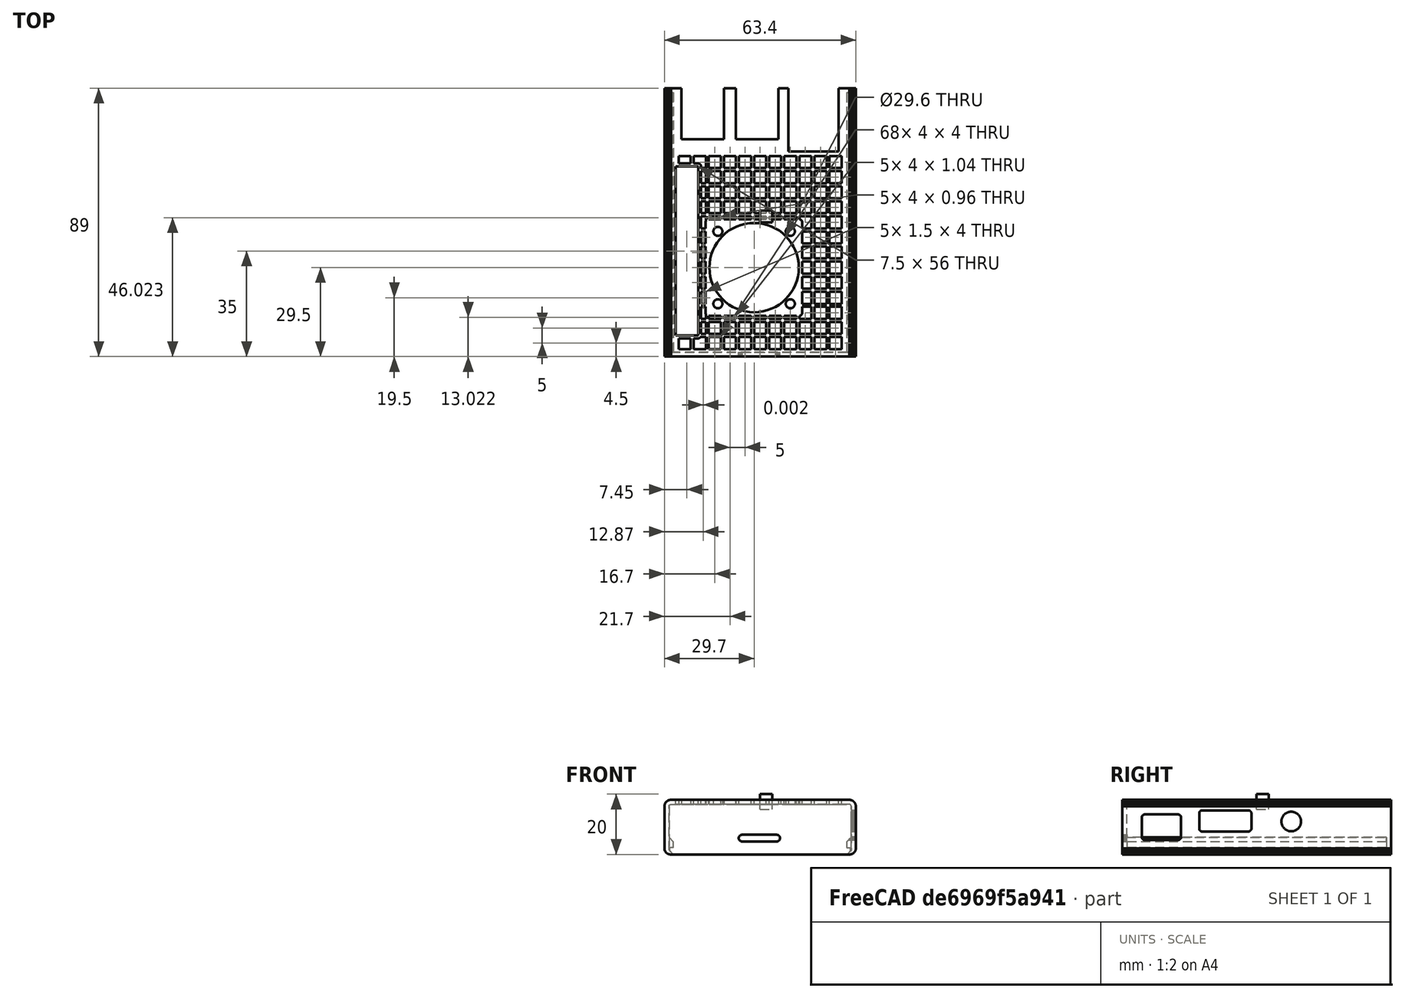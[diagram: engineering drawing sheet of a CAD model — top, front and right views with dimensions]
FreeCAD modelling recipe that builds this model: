
FCSTD DOCUMENT  (FreeCAD 0.14R3702 (Git))
Label: mi_raspberry_case
License: CC-BY 3.0
LicenseURL: http://creativecommons.org/licenses/by/3.0/
objects: Part::Feature×7, Part::MultiFuse×7, Part::Box×5, Mesh::Feature×3, Part::Offset×2, Part::Cut×2, Part::MultiCommon×1, Part::Cylinder×1, Part::FeaturePython×1
note: 26 computed .brp shape members not serialized (recipe doc carries the construction recipe); baked Part::Feature solids carry a one-line shape summary decoded from their .brp

FEATURE [Mesh::Feature] Raspberry_Pi_2_Case_v1_0___Cover  label="Raspberry_Pi_2_Case_v1.0_-_Cover"
FEATURE [Mesh::Feature] COVER_FAN_30X30
  Placement = pos=(-2,-15,18) rot=(0,0,1;0rad)
FEATURE [Mesh::Feature] B__Model_v4  label="B+_Model_v4"
  Placement = pos=(70.5,97,2) rot=(0,0,1;1.5708rad)
FEATURE [Part::Feature] Raspberry_Pi_2_Case_v1_0___Cover001
  shape: bbox 63.4 x 89 x 18.1 mm, 3440 faces, 0 solids (baked)
FEATURE [Part::Feature] Raspberry_Pi_2_Case_v1_0___Cover001001  label="Raspberry_Pi_2_Case_v1_0___Cover002"
  shape: bbox 63.4 x 89 x 18.1 mm, 1022 faces, 0 solids (baked)
FEATURE [Part::Feature] Raspberry_Pi_2_Case_v1_0___Cover001001_solid  label="Raspberry_Pi_2_Case_v1_0___Cover002 (Solid)"
  shape: bbox 63.4 x 89 x 18.1 mm, 1022 faces (baked)
FEATURE [Part::Box] Box  label="hueco gpio"
  Height = 5
  Length = 7.5
  Placement = pos=(-28,-37.5,13) rot=(0,0,1;0rad)
  Width = 56
FEATURE [Part::Box] Box001  label="caja ventilador"
  Height = 5
  Length = 30
  Placement = pos=(-17,-30,13) rot=(0,0,1;0rad)
  Width = 30
FEATURE [Part::Feature] Part__Feature  label="Chamfer001"
  Placement = pos=(-14,-3,20) rot=(0,0,1;0rad)
  shape: bbox 5.5 x 5.5 x 15 mm, 16 faces (baked)
FEATURE [Part::Feature] Part__Feature001  label="Chamfer002"
  Placement = pos=(10,-3,20) rot=(0,0,1;0rad)
  shape: bbox 5.5 x 5.5 x 15 mm, 16 faces (baked)
FEATURE [Part::MultiFuse] Fusion
  Shapes = -> [Part__Feature001,Part__Feature]
FEATURE [Part::Feature] Part__Feature002  label="Chamfer003"
  Placement = pos=(-14,-3,20) rot=(0,0,1;0rad)
  shape: bbox 5.5 x 5.5 x 15 mm, 16 faces (baked)
FEATURE [Part::Feature] Part__Feature003  label="Chamfer004"
  Placement = pos=(10,-3,20) rot=(0,0,1;0rad)
  shape: bbox 5.5 x 5.5 x 15 mm, 16 faces (baked)
FEATURE [Part::MultiFuse] Fusion001
  Placement = pos=(0,-24,0) rot=(0,0,1;0rad)
  Shapes = -> [Part__Feature003,Part__Feature002]
FEATURE [Part::MultiFuse] Fusion002  label="tornillos"
  Shapes = -> [Fusion001,Fusion]
FEATURE [Part::Box] Box002  label="Cubo"
  Height = 5
  Length = 4
  Placement = pos=(0,0,13) rot=(0,0,1;0rad)
  Width = 4
FEATURE [Part::Box] Box003  label="hueco gpio001"
  Height = 5
  Length = 7.5
  Placement = pos=(-28,-37.5,13) rot=(0,0,1;0rad)
  Width = 56
FEATURE [Part::Offset] Offset
  Fill = false
  Intersection = false
  Join = 0
  Mode = 0
  SelfIntersection = false
  Source = -> Box003
  Value = 1
FEATURE [Part::Offset] Offset001
  Fill = false
  Intersection = false
  Join = 0
  Mode = 0
  SelfIntersection = false
  Source = -> Box001
  Value = 1
FEATURE [Part::MultiFuse] Fusion003
  Placement = pos=(0,0,0) rot=(-0.492564,-0.865775,-0.088399;0.004943rad)
  Shapes = -> [Offset001,Offset]
FEATURE [Part::MultiCommon] Common
  Shapes = -> [Raspberry_Pi_2_Case_v1_0___Cover001001_solid,Fusion003]
FEATURE [Part::Cylinder] Cylinder  label="Cilindro"
  Angle = 360
  Height = 5
  Placement = pos=(-2,-15,13) rot=(0,0,1;0rad)
  Radius = 14.8
FEATURE [Part::MultiFuse] Fusion004  label="hueco_ventilador"
  Shapes = -> [Cylinder,Fusion002]
FEATURE [Part::Box] Box004  label="Cubo001"
  Height = 5
  Length = 4
  Placement = pos=(-27,-41,13) rot=(0,0,1;0rad)
  Width = 4
FEATURE [Part::FeaturePython] Array  # Draft array (typed FeaturePython)
  Angle = 360
  ArrayType = 0
  Axis = (0,0,1)
  Base = -> Box004
  Center = (0,0,0)
  IntervalX = (5,0,0)
  IntervalY = (0,5,0)
  IntervalZ = (0,0,1)
  NumberPolar = 1
  NumberX = 11
  NumberY = 13
  NumberZ = 1
  Placement = pos=(0,-1,0) rot=(0,0,1;0rad)
FEATURE [Part::Cut] Cut
  Base = -> Raspberry_Pi_2_Case_v1_0___Cover001001_solid
  Tool = -> Array
FEATURE [Part::MultiFuse] Fusion005
  Shapes = -> [Common,Cut]
FEATURE [Part::MultiFuse] Fusion006
  Shapes = -> [Fusion004,Box]
FEATURE [Part::Cut] Cut001
  Base = -> Fusion005
  Tool = -> Fusion006
